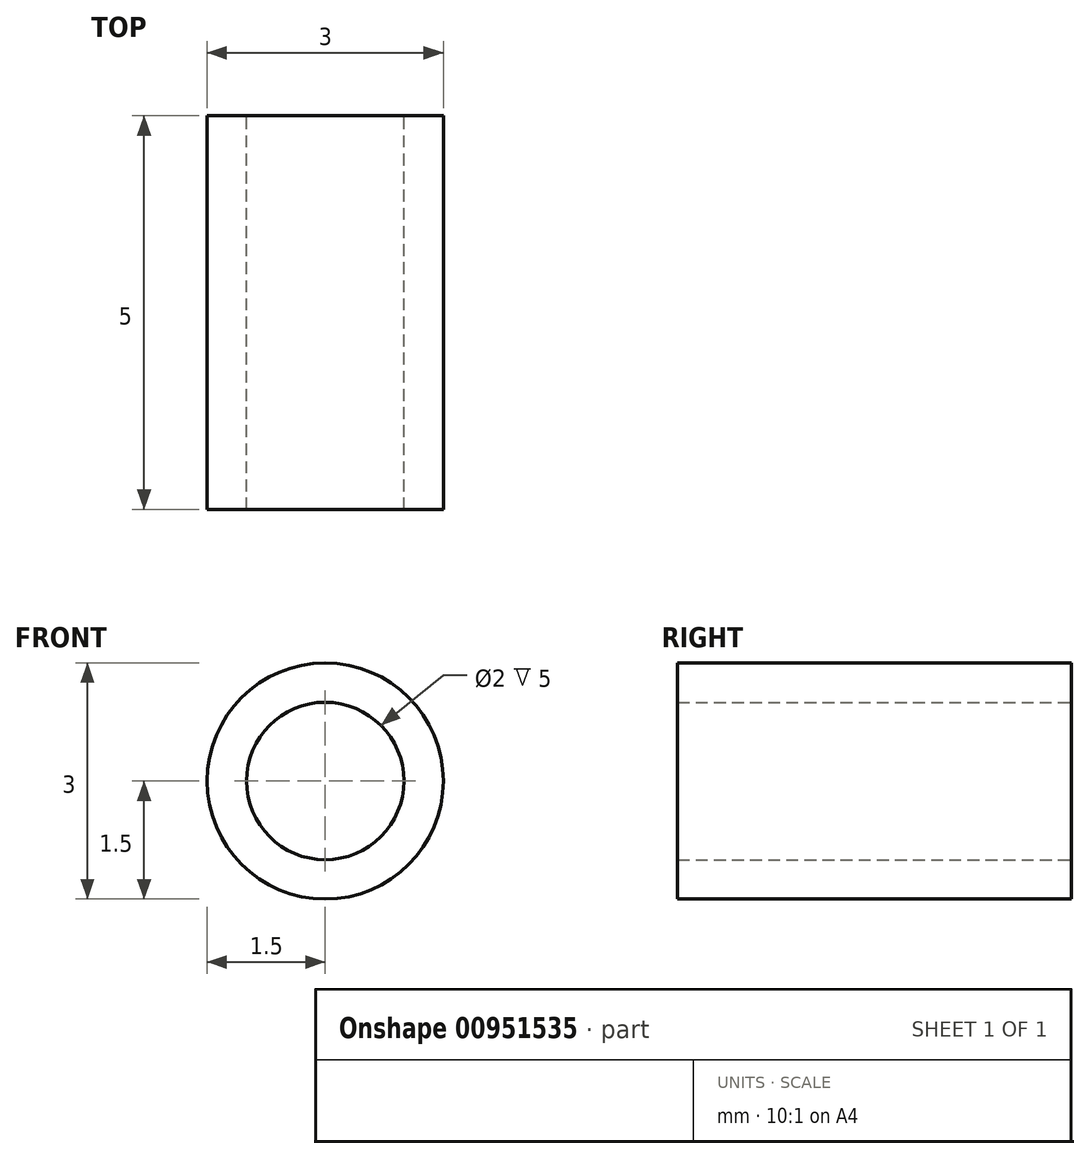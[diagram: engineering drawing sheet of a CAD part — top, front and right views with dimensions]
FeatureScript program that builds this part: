
annotation { "Feature Type Name" : "Feature", "Feature Type Description" : "" }
export const myFeature = defineFeature(function(context is Context, id is Id, definition is map)
    precondition{}
    {
        {
            var Q0;
            Q0=qCreatedBy(makeId("Front.planeOp"),FACE);
            var sketch = newSketch(context, id + "F0", { "sketchPlane" : qUnion([Q0])});
            skCircle(sketch, "E0", {"center": v(0, 0) * mm, "radius": 1.5 * mm});
            skCircle(sketch, "E1", {"center": v(0, 0) * mm, "radius": 1 * mm});
            skSolve(sketch);
        }
        {
            var Q0;
            Q0 = qSketchRegion(id + "F0", true);
            extrude(context, id + "F1", {"entities" : qUnion([Q0]), "depth" : 5 * mm, "offsetDistance" : 25 * mm});
        }
    });
